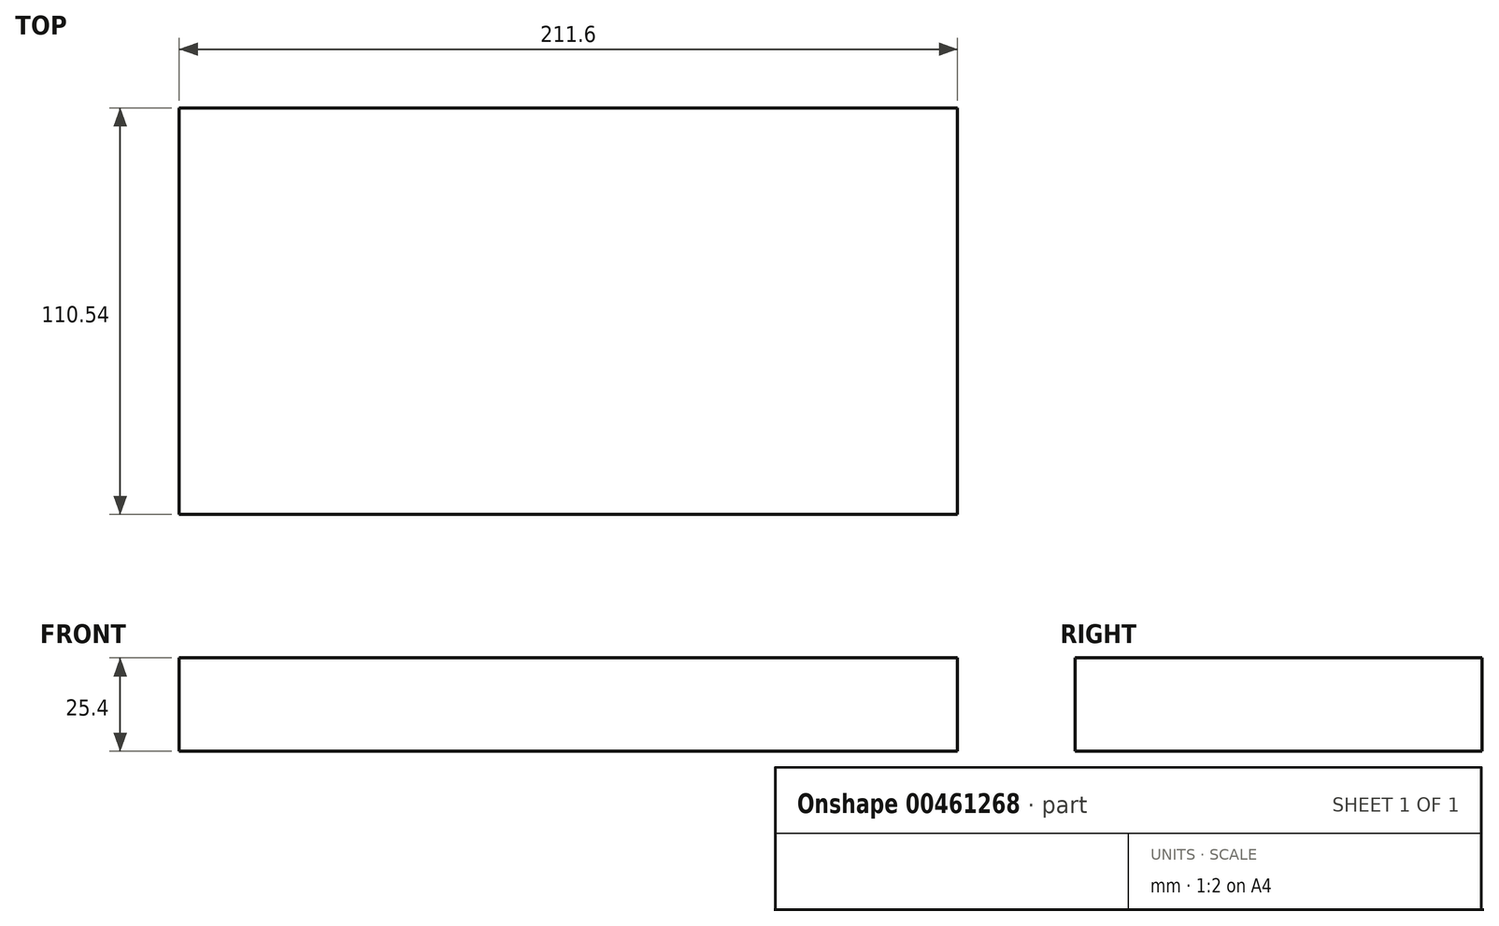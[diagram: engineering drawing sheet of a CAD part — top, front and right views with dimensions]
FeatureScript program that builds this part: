
annotation { "Feature Type Name" : "Feature", "Feature Type Description" : "" }
export const myFeature = defineFeature(function(context is Context, id is Id, definition is map)
    precondition{}
    {
        {
            var Q0;
            Q0=qCreatedBy(makeId("Top.planeOp"),FACE);
            var sketch = newSketch(context, id + "F0", { "sketchPlane" : qUnion([Q0])});
            skLineSegment(sketch, "E0.bottom", {"start": v(-129.24, 59.77) * mm, "end": v(82.36, 59.77) * mm});
            skLineSegment(sketch, "E0.top", {"start": v(-129.24, -50.77) * mm, "end": v(82.36, -50.77) * mm});
            skLineSegment(sketch, "E0.left", {"start": v(-129.24, 59.77) * mm, "end": v(-129.24, -50.77) * mm});
            skLineSegment(sketch, "E0.right", {"start": v(82.36, 59.77) * mm, "end": v(82.36, -50.77) * mm});
            skSolve(sketch);
        }
        {
            var Q0;
            Q0 = qSketchRegion(id + "F0", true);
            var Q1;
            Q1=makeQuery(id+"F0.imprint","IMPRINT",FACE,{"disambiguationData":[TD([[makeQuery(id+"F0.imprint","IMPRINT",EDGE,{"derivedFrom":sQuery(id+"F0.wireOp",EDGE,"E0.bottom")}),-1.0]])]});
            extrude(context, id + "F1", {"entities" : qUnion([Q0, Q1]), "depth" : 25.4 * mm, "offsetDistance" : 25.4 * mm});
        }
    });
